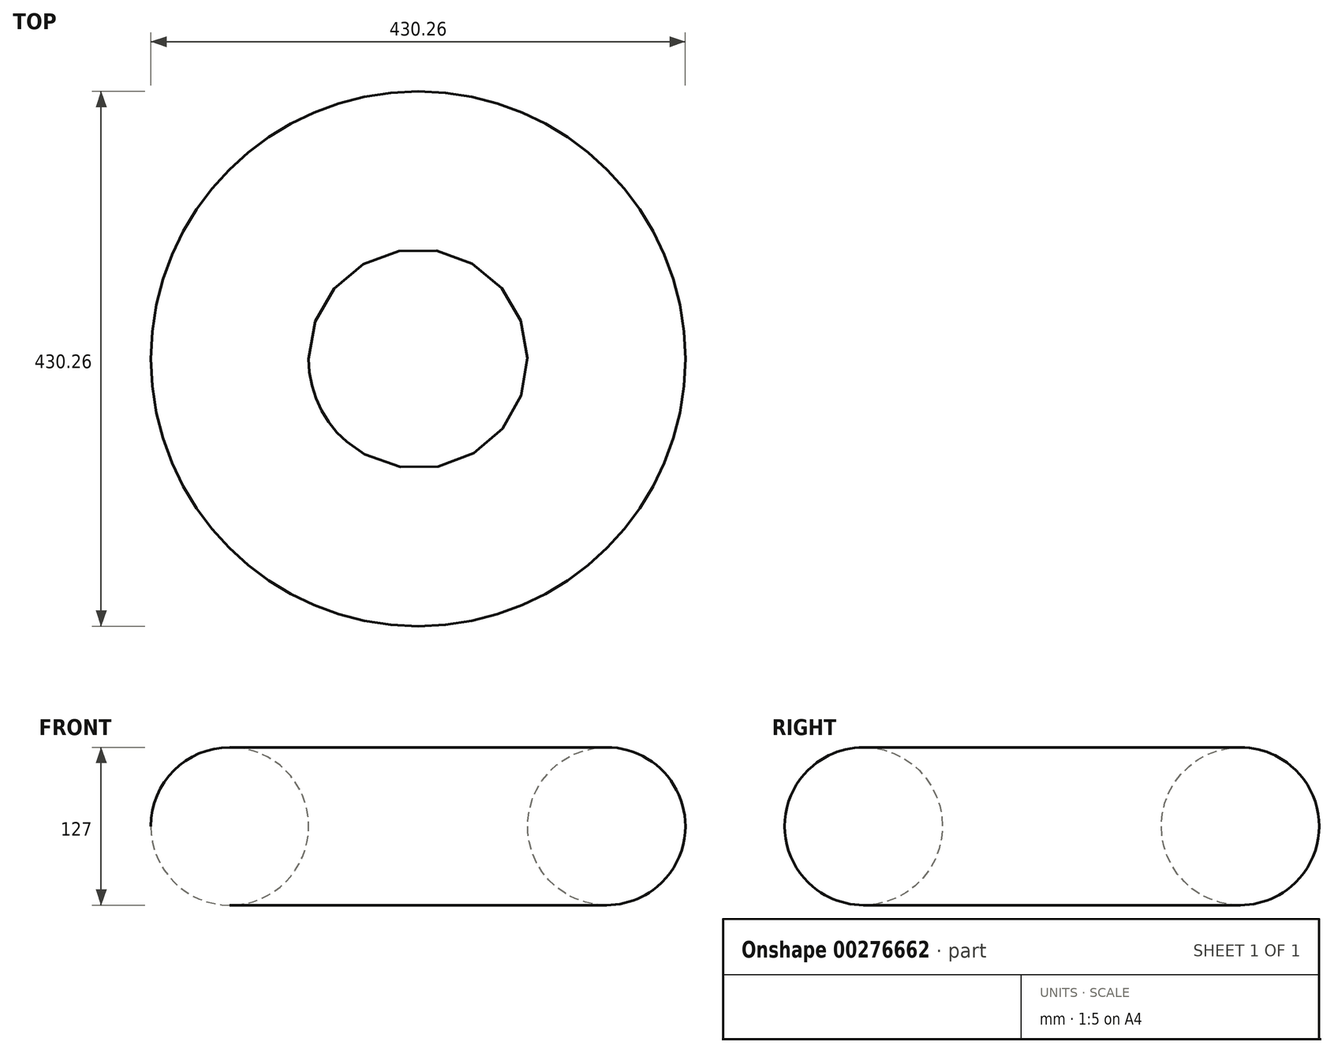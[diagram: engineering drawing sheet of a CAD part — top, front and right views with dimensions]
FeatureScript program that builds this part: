
annotation { "Feature Type Name" : "Feature", "Feature Type Description" : "" }
export const myFeature = defineFeature(function(context is Context, id is Id, definition is map)
    precondition{}
    {
        {
            var Q0;
            Q0=qCreatedBy(makeId("Front.planeOp"),FACE);
            var sketch = newSketch(context, id + "F0", { "sketchPlane" : qUnion([Q0])});
            skLineSegment(sketch, "E0", {"start": v(0, 0) * mm, "end": v(0, 218.14) * mm, "construction": true});
            skCircle(sketch, "E1", {"center": v(151.63, 100.2) * mm, "radius": 63.5 * mm});
            skSolve(sketch);
        }
        {
            var Q0;
            Q0 = qSketchRegion(id + "F0", true);
            var Q1;
            Q1=sQuery(id+"F0.wireOp",EDGE,"E0");
            revolve(context, id + "F1", {"entities" : qUnion([Q0]), "axis" : qUnion([Q1]), "revolveType" : RevolveType.FULL});
        }
    });
